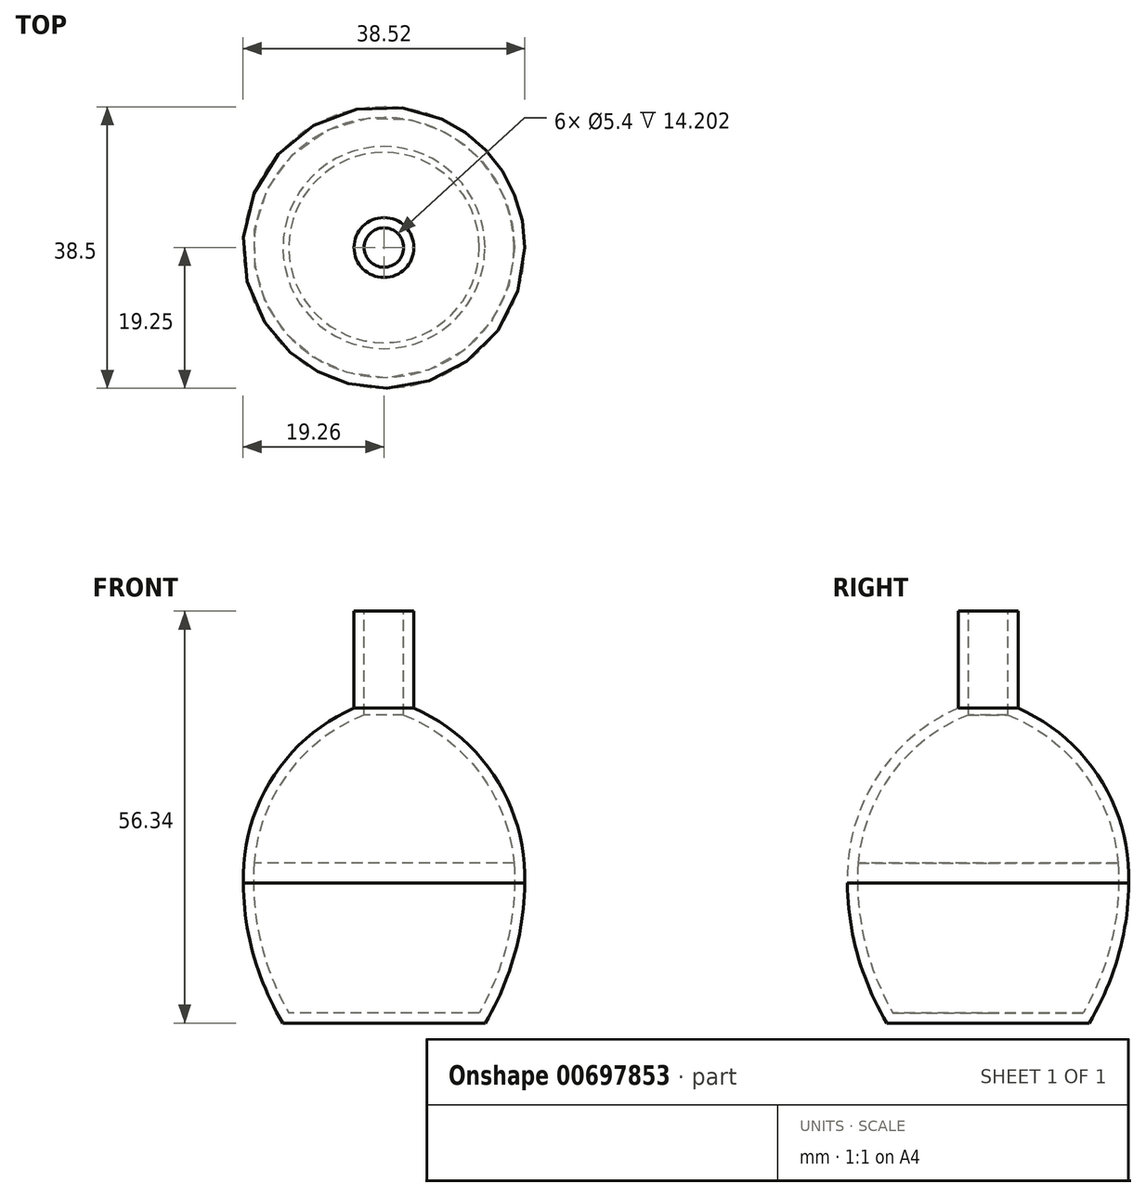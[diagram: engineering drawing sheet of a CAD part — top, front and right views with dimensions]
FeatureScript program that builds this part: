
annotation { "Feature Type Name" : "Feature", "Feature Type Description" : "" }
export const myFeature = defineFeature(function(context is Context, id is Id, definition is map)
    precondition{}
    {
        {
            var Q0;
            Q0=qCreatedBy(makeId("Front.planeOp"),FACE);
            var sketch = newSketch(context, id + "F0", { "sketchPlane" : qUnion([Q0])});
            skLineSegment(sketch, "E0", {"start": v(4.1, 56.34) * mm, "end": v(4.1, 43.08) * mm});
            skArc(sketch, "E1", {"start": v(19.25, 19.14) * mm, "mid": v(15.34, 33.42) * mm, "end": v(4.1, 43.08) * mm});
            skArc(sketch, "E2", {"start": v(13.82, 0) * mm, "mid": v(17.82, 9.2) * mm, "end": v(19.25, 19.14) * mm});
            skLineSegment(sketch, "E3", {"start": v(13.82, 0) * mm, "end": v(0, 0) * mm});
            skLineSegment(sketch, "E4", {"start": v(4.1, 56.34) * mm, "end": v(2.7, 56.34) * mm});
            skLineSegment(sketch, "E5.0", {"start": v(13.02, 1.4) * mm, "end": v(0, 1.4) * mm});
            skArc(sketch, "E5.1", {"start": v(13.02, 1.4) * mm, "mid": v(16.9, 11.29) * mm, "end": v(17.78, 21.87) * mm});
            skArc(sketch, "E5.2", {"start": v(17.78, 21.87) * mm, "mid": v(13.13, 34.16) * mm, "end": v(2.7, 42.14) * mm});
            skLineSegment(sketch, "E5.3", {"start": v(2.7, 56.34) * mm, "end": v(2.7, 42.14) * mm});
            skLineSegment(sketch, "E6", {"start": v(0, 1.4) * mm, "end": v(0, 0) * mm});
            skLineSegment(sketch, "E7", {"start": v(4.1, 56.34) * mm, "end": v(0, 56.34) * mm, "construction": true});
            skSolve(sketch);
        }
        {
            var Q0;
            Q0 = qSketchRegion(id + "F0", true);
            var Q1;
            Q1=sQuery(id+"F0.wireOp",EDGE,"E6");
            revolve(context, id + "F1", {"surfaceOperationType" : NewSurfaceOperationType.NEW, "entities" : qUnion([Q0]), "axis" : qUnion([Q1]), "revolveType" : RevolveType.FULL});
        }
    });
